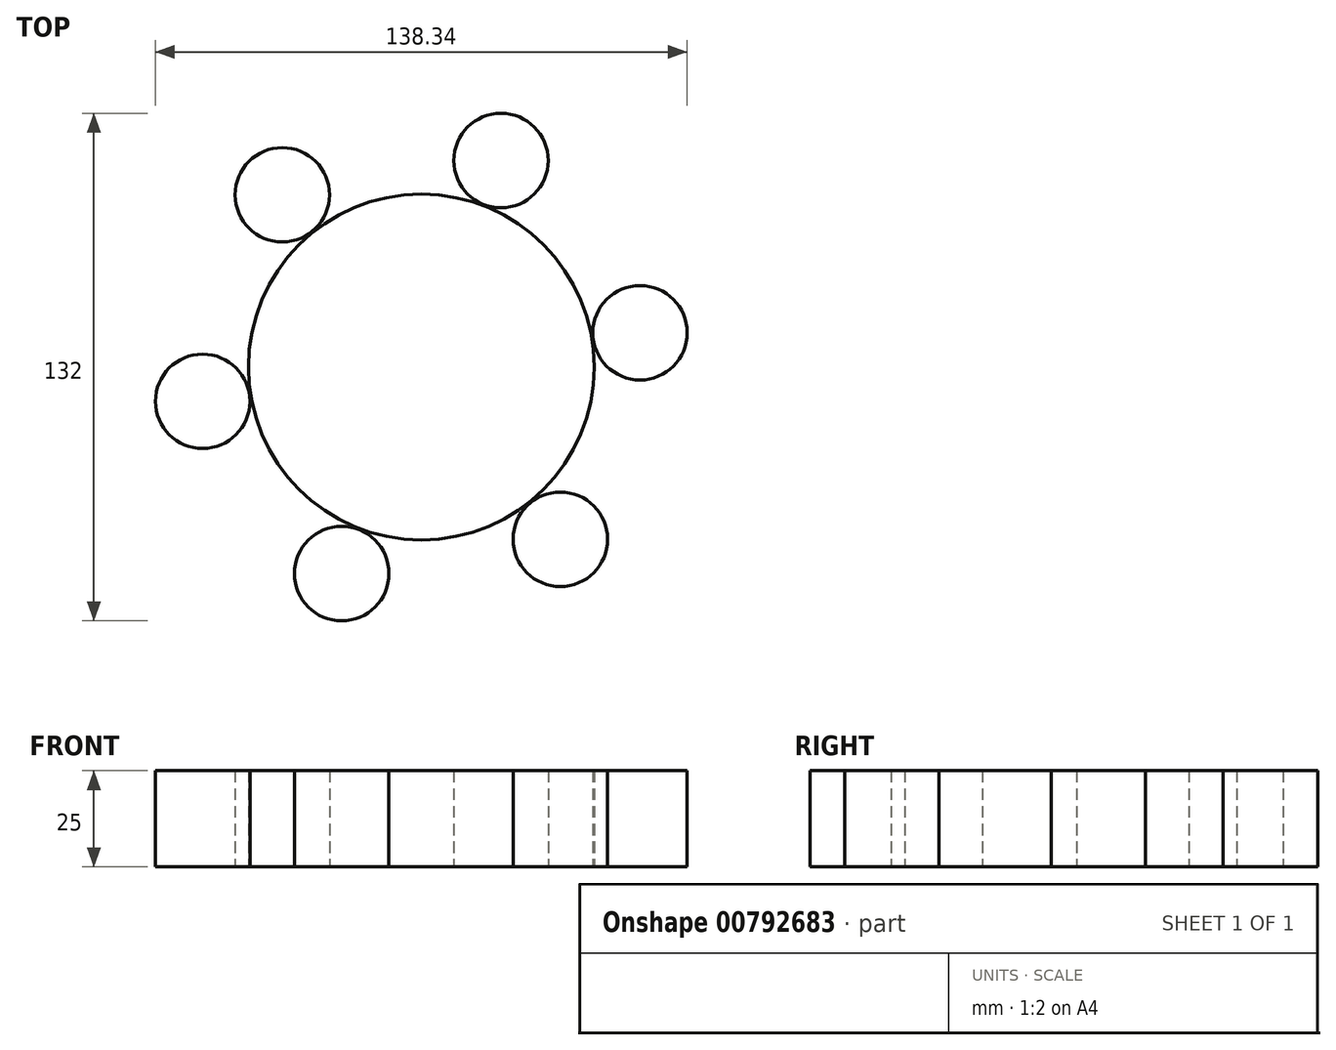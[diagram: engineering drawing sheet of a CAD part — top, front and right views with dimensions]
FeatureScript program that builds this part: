
annotation { "Feature Type Name" : "Feature", "Feature Type Description" : "" }
export const myFeature = defineFeature(function(context is Context, id is Id, definition is map)
    precondition{}
    {
        {
            var Q0;
            Q0=qCreatedBy(makeId("Top.planeOp"),FACE);
            var sketch = newSketch(context, id + "F0", { "sketchPlane" : qUnion([Q0])});
            skCircle(sketch, "E0", {"center": v(0, 0) * mm, "radius": 44.97 * mm});
            skSolve(sketch);
        }
        {
            var Q0;
            Q0=makeQuery(id+"F0.imprint","IMPRINT",FACE,{"disambiguationData":[TD([[makeQuery(id+"F0.imprint","IMPRINT",EDGE,{"derivedFrom":sQuery(id+"F0.wireOp",EDGE,"E0")}),1.0]])]});
            extrude(context, id + "F1", {"entities" : qUnion([Q0]), "depth" : 25 * mm, "offsetDistance" : 25 * mm});
        }
        {
            var Q0;
            Q0=qCreatedBy(makeId("Top.planeOp"),FACE);
            var sketch = newSketch(context, id + "F2", { "sketchPlane" : qUnion([Q0])});
            skCircle(sketch, "E1", {"center": v(56.89, 8.92) * mm, "radius": 12.28 * mm});
            skSolve(sketch);
        }
        {
            var Q0;
            Q0=makeQuery(id+"F2.imprint","IMPRINT",FACE,{"disambiguationData":[TD([[makeQuery(id+"F2.imprint","IMPRINT",EDGE,{"derivedFrom":sQuery(id+"F2.wireOp",EDGE,"E1")}),1.0]])]});
            extrude(context, id + "F3", {"entities" : qUnion([Q0]), "depth" : 25 * mm, "offsetDistance" : 25 * mm});
        }
        {
            var Q0;
            Q0=makeQuery(id+"F3.opExtrude","SWEPT_BODY",BODY,{"disambiguationData":[OSD([sQuery(id+"F2.wireOp",EDGE,"E1")])]});
            var Q1;
            Q1=makeQuery(id+"F1.opExtrude","CAP_EDGE",EDGE,{"disambiguationData":[OSD([sQuery(id+"F0.wireOp",EDGE,"E0")])],"isStart":false});
            circularPattern(context, id + "F4", {"entities" : qUnion([Q0]), "axis" : qUnion([Q1]), "angle" : 360 * degree, "instanceCount" : 6, "equalSpace" : true});
        }
    });
